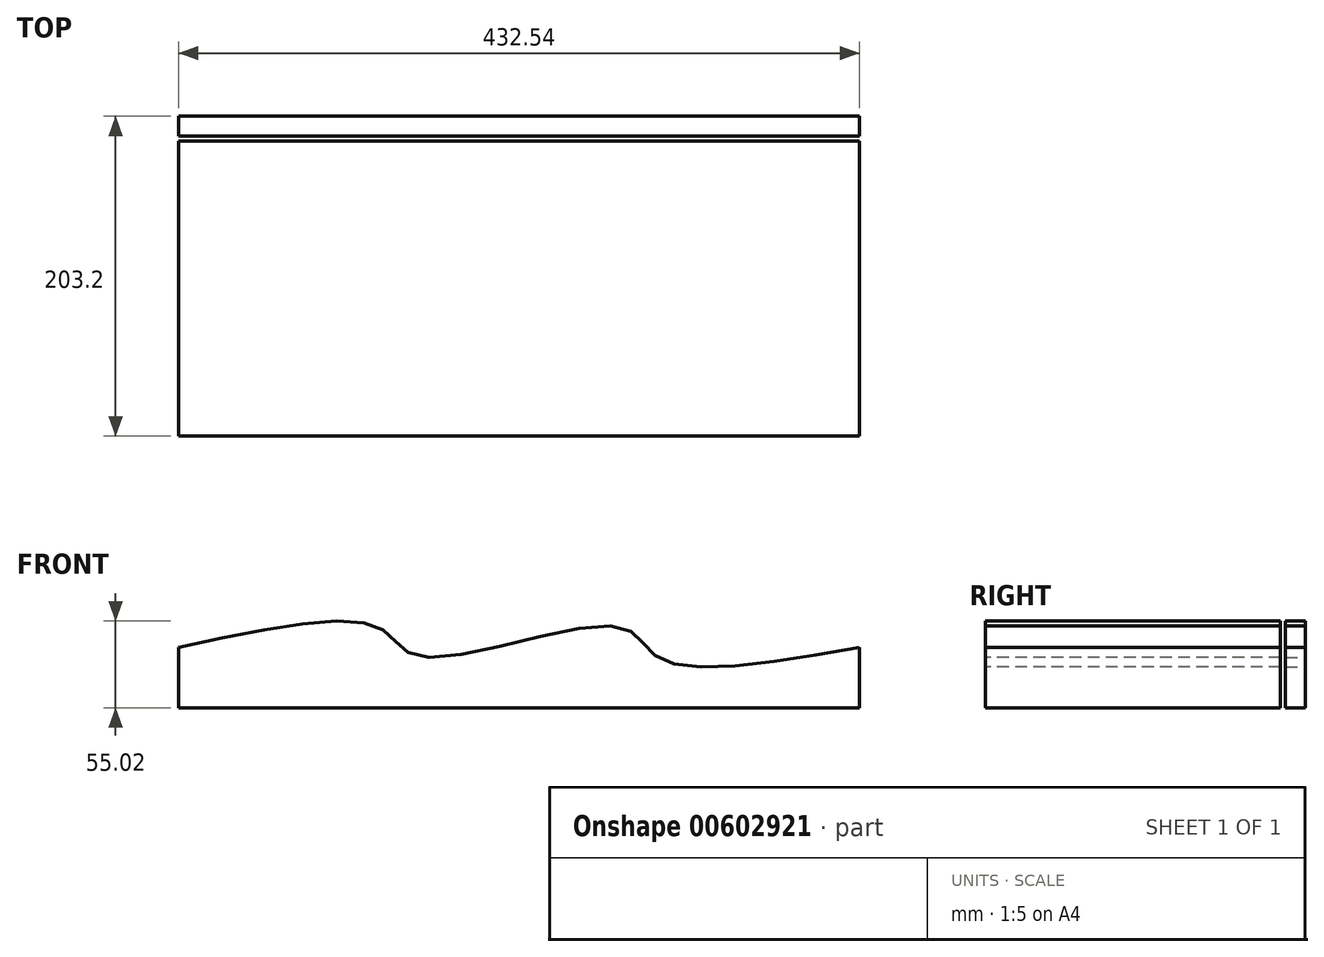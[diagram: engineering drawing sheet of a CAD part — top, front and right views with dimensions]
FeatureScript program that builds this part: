
annotation { "Feature Type Name" : "Feature", "Feature Type Description" : "" }
export const myFeature = defineFeature(function(context is Context, id is Id, definition is map)
    precondition{}
    {
        {
            var Q0;
            Q0=qCreatedBy(makeId("Front.planeOp"),FACE);
            var sketch = newSketch(context, id + "F0", { "sketchPlane" : qUnion([Q0])});
            skLineSegment(sketch, "E0", {"start": v(-295.52, 38.23) * mm, "end": v(-295.52, 0) * mm});
            skLineSegment(sketch, "E1", {"start": v(-295.52, 0) * mm, "end": v(137.02, 0) * mm});
            skLineSegment(sketch, "E2", {"start": v(137.02, 0) * mm, "end": v(137.02, 38.23) * mm});
            skFitSpline(sketch, "E3", {"points": [v(-295.52, 38.23) * mm, v(-168.18, 50.86) * mm, v(-142.4, 32.44) * mm, v(-15.58, 51.39) * mm, v(9.68, 31.4) * mm, v(137.02, 38.23) * mm], "startDerivative": vector(640.5, 139.24) * mm, "endDerivative": vector(643.71, 112.5) * mm});
            skSolve(sketch);
        }
        {
            var Q0;
            Q0=makeQuery(id+"F0.imprint","IMPRINT",FACE,{"disambiguationData":[TD([[makeQuery(id+"F0.imprint","IMPRINT",EDGE,{"derivedFrom":sQuery(id+"F0.wireOp",EDGE,"E0")}),1.0]])]});
            extrude(context, id + "F1", {"entities" : qUnion([Q0]), "depth" : 203.2 * mm, "offsetDistance" : 25.4 * mm});
        }
        {
            var Q0;
            Q0=makeQuery(id+"F1.opExtrude","SWEPT_FACE",FACE,{"disambiguationData":[OSD([sQuery(id+"F0.wireOp",EDGE,"E1")])]});
            var sketch = newSketch(context, id + "F2", { "sketchPlane" : qUnion([Q0])});
            skLineSegment(sketch, "E4", {"start": v(-295.52, 12.7) * mm, "end": v(137.02, 12.7) * mm});
            skLineSegment(sketch, "E5", {"start": v(137.02, 15.88) * mm, "end": v(-295.52, 15.87) * mm});
            skLineSegment(sketch, "E6", {"start": v(-295.52, 15.87) * mm, "end": v(-295.52, 12.7) * mm});
            skLineSegment(sketch, "E7", {"start": v(137.02, 15.88) * mm, "end": v(137.02, 12.7) * mm});
            skSolve(sketch);
        }
        {
            var Q0;
            Q0=makeQuery(id+"F2.imprint","IMPRINT",FACE,{"disambiguationData":[TD([[makeQuery(id+"F2.imprint","IMPRINT",EDGE,{"derivedFrom":sQuery(id+"F2.wireOp",EDGE,"E4")}),1.0]])]});
            var Q1;
            Q1=makeQuery(id+"F1.opExtrude","SWEPT_BODY",BODY,{"disambiguationData":[OSD([sQuery(id+"F0.wireOp",EDGE,"E0"),sQuery(id+"F0.wireOp",EDGE,"E1"),sQuery(id+"F0.wireOp",EDGE,"E2"),sQuery(id+"F0.wireOp",EDGE,"E3")])]});
            extrude(context, id + "F3", {"entities" : qUnion([Q0]), "operationType" : NewBodyOperationType.REMOVE, "endBound" : BoundingType.UP_TO_NEXT, "oppositeDirection" : true, "depth" : 25.4 * mm, "endBoundEntityBody" : qUnion([Q1]), "offsetDistance" : 9.52 * mm, "offsetOppositeDirection" : true});
        }
    });
